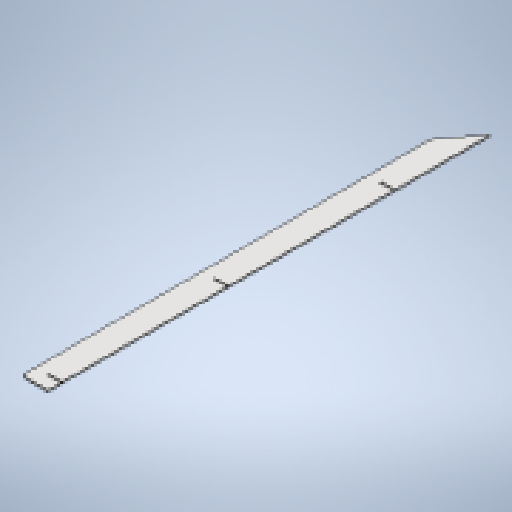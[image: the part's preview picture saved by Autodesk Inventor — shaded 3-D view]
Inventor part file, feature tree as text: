
AUTODESK INVENTOR PART (.ipt)
format: ipt  version: 2025 (Build 290162010, 162A)  size: 333,824 bytes
history: native  units: mm
features: other x4, sketch x3, chamfer x2, sheet_metal_op x1, extrude x1, pattern_linear x1
ambient origin geometry x8: Origin, YZ Plane, XZ Plane, XY Plane, X Axis, Y Axis, Z Axis, Center Point
bodies: Solid1 (feature_tree)
feature tree (12):
  sheet_metal_op  "Face1"
  other  "Corner Chamfer2"
  chamfer  "Corner Round1"
  extrude  "Extrusion1"  Depth=860.0mm
  pattern_linear  "Rectangular Pattern1"  Spacing1=9.372418mm  [1 undecoded]
  chamfer  "Corner Round3"
  other  "Mark1"
  sketch  "Sketch1"  dims[d0=50.0mm d1=860.0mm]
  other  "Plate1"
  sketch  "Sketch2"  dims[d2=3.0mm]
  sketch  "Sketch3"  dims[d5=9.372418mm d6=9.372418mm d10=3.0mm d11=6.0mm d12=45.0deg d13=6.0mm d15=188.0mm d16=26.0mm d17=3.0mm d18=0.0mm d19=0.0mm d20=30.0mm d22=323.0mm d23=6.0mm]
  other  "Definition1"
note: 1 required parameter value undecoded (feature->parameter linkage not recoverable at this tier; creation-order binding heuristic only, values carry confidence <= 0.55)
